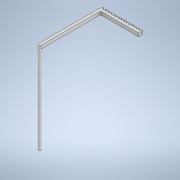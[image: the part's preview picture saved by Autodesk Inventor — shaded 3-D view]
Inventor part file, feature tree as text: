
AUTODESK INVENTOR PART (.ipt)
format: ipt  version: 2021 (Build 250183000, 183)  size: 222,720 bytes
history: native  units: in
note: dims shown in document units (in); Inventor stores cm internally (conversion verified against a paired STEP export)
features: extrude x2, fillet x2, sketch x2
ambient origin geometry x8: Origin, YZ Plane, XZ Plane, XY Plane, X Axis, Y Axis, Z Axis, Center Point
bodies: Solid1 (feature_tree), Solid2 (feature_tree)
feature tree (6):
  extrude  "Extrusion4"  Depth=0.4724in
  extrude  "Extrusion5"  Depth=0.3937in
  fillet  "Fillet1"  Radius=12.5984in
  fillet  "Fillet2"  Radius=0.1969in
  sketch  "Sketch4"  dims[d14=0.4724in d15=9.1063in]
  sketch  "Sketch5"  dims[d16=0.3937in d17=0.0in d18=0.3937in d19=12.5984in d20=0.0in d21=0.1969in d22=0.1969in d3=0.0197in d4=1.9685in d5=0.0197in d6=1.9685in]
